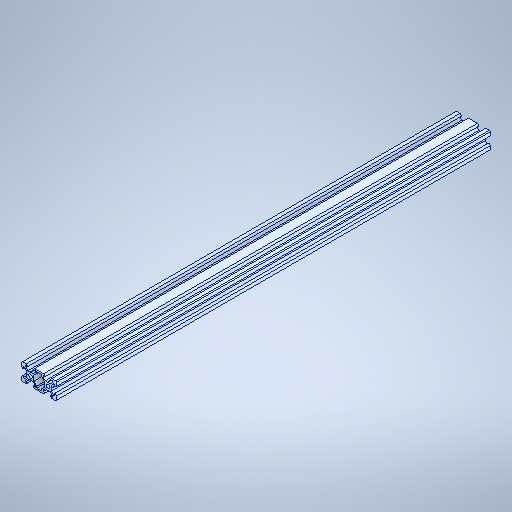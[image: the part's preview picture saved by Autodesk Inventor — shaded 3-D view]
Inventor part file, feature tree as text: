
AUTODESK INVENTOR PART (.ipt)
format: ipt  version: 2025.1 (Build 291241020, 241B)  size: 545,792 bytes
history: native  units: in
note: dims shown in document units (in); Inventor stores cm internally (conversion verified against a paired STEP export)
features: projected_geometry x102, plane x1, extrude x1, sketch x1
ambient origin geometry x8: Origin, YZ Plane, XZ Plane, XY Plane, X Axis, Y Axis, Z Axis, Center Point
bodies: Solid1 (feature_tree)
feature tree (105):
  plane  "Work Plane2"
  extrude  "Extrusion1"  [1 undecoded]
  sketch  "Sketch1"  dims[d0=19.685in d1=0.0in]
  projected_geometry  "Projected Loop1"
  projected_geometry  "Projected Loop2"
  projected_geometry  "Projected Loop3"
  projected_geometry  "Projected Loop4"
  projected_geometry  "Projected Loop5"
  projected_geometry  "Projected Loop6"
  projected_geometry  "Projected Loop7"
  projected_geometry  "Projected Loop8"
  projected_geometry  "Projected Loop9"
  projected_geometry  "Projected Loop10"
  projected_geometry  "Projected Loop11"
  projected_geometry  "Projected Loop12"
  projected_geometry  "Projected Loop13"
  projected_geometry  "Projected Loop14"
  projected_geometry  "Projected Loop15"
  projected_geometry  "Projected Loop16"
  projected_geometry  "Projected Loop17"
  projected_geometry  "Projected Loop18"
  projected_geometry  "Projected Loop19"
  projected_geometry  "Projected Loop20"
  projected_geometry  "Projected Loop21"
  projected_geometry  "Projected Loop22"
  projected_geometry  "Projected Loop23"
  projected_geometry  "Projected Loop24"
  projected_geometry  "Projected Loop25"
  projected_geometry  "Projected Loop26"
  projected_geometry  "Projected Loop27"
  projected_geometry  "Projected Loop28"
  projected_geometry  "Projected Loop29"
  projected_geometry  "Projected Loop30"
  projected_geometry  "Projected Loop31"
  projected_geometry  "Projected Loop32"
  projected_geometry  "Projected Loop33"
  projected_geometry  "Projected Loop34"
  projected_geometry  "Projected Loop35"
  projected_geometry  "Projected Loop36"
  projected_geometry  "Projected Loop37"
  projected_geometry  "Projected Loop38"
  projected_geometry  "Projected Loop39"
  projected_geometry  "Projected Loop40"
  projected_geometry  "Projected Loop41"
  projected_geometry  "Projected Loop42"
  projected_geometry  "Projected Loop43"
  projected_geometry  "Projected Loop44"
  projected_geometry  "Projected Loop45"
  projected_geometry  "Projected Loop46"
  projected_geometry  "Projected Loop47"
  projected_geometry  "Projected Loop48"
  projected_geometry  "Projected Loop49"
  projected_geometry  "Projected Loop50"
  projected_geometry  "Projected Loop51"
  projected_geometry  "Projected Loop52"
  projected_geometry  "Projected Loop53"
  projected_geometry  "Projected Loop54"
  projected_geometry  "Projected Loop55"
  projected_geometry  "Projected Loop56"
  projected_geometry  "Projected Loop57"
  projected_geometry  "Projected Loop58"
  projected_geometry  "Projected Loop59"
  projected_geometry  "Projected Loop60"
  projected_geometry  "Projected Loop61"
  projected_geometry  "Projected Loop62"
  projected_geometry  "Projected Loop63"
  projected_geometry  "Projected Loop64"
  projected_geometry  "Projected Loop65"
  projected_geometry  "Projected Loop66"
  projected_geometry  "Projected Loop67"
  projected_geometry  "Projected Loop68"
  projected_geometry  "Projected Loop69"
  projected_geometry  "Projected Loop70"
  projected_geometry  "Projected Loop71"
  projected_geometry  "Projected Loop72"
  projected_geometry  "Projected Loop73"
  projected_geometry  "Projected Loop74"
  projected_geometry  "Projected Loop75"
  projected_geometry  "Projected Loop76"
  projected_geometry  "Projected Loop77"
  projected_geometry  "Projected Loop78"
  projected_geometry  "Projected Loop79"
  projected_geometry  "Projected Loop80"
  projected_geometry  "Projected Loop81"
  projected_geometry  "Projected Loop82"
  projected_geometry  "Projected Loop83"
  projected_geometry  "Projected Loop84"
  projected_geometry  "Projected Loop85"
  projected_geometry  "Projected Loop86"
  projected_geometry  "Projected Loop87"
  projected_geometry  "Projected Loop88"
  projected_geometry  "Projected Loop89"
  projected_geometry  "Projected Loop90"
  projected_geometry  "Projected Loop91"
  projected_geometry  "Projected Loop92"
  projected_geometry  "Projected Loop93"
  projected_geometry  "Projected Loop94"
  projected_geometry  "Projected Loop95"
  projected_geometry  "Projected Loop96"
  projected_geometry  "Projected Loop97"
  projected_geometry  "Projected Loop98"
  projected_geometry  "Projected Loop99"
  projected_geometry  "Projected Loop100"
  projected_geometry  "Projected Loop101"
  projected_geometry  "Projected Loop102"
note: 1 required parameter value undecoded (feature->parameter linkage not recoverable at this tier; creation-order binding heuristic only, values carry confidence <= 0.55)
